# Revit family: Hager-Panelboard_Invicta_3_(630A-800A_Inc_125A_Out)-NoHosted-UK-en
name_source: partatom
category: Electrical Equipment
units: mm (PartAtom-declared; Revit-internal decimal feet)

## family parameters
Always vertical = Yes
Cut with Voids When Loaded = No
Panel Configuration = Two Columns, Circuits Across
Part Type = Panelboard
Room Calculation Point = No
Round Connector Dimension = Use Diameter
Shared = No
Work Plane-Based = Yes

## types (6) — shared parameters
Classification.Uniclass.Pr.Description = Control circuit device enclosures
Classification.Uniclass.Pr.Number = Pr_80_77_28_16
Default Elevation = 1219 mm
EF000003 - Mounting method = EV000384 - Surface mounted (plaster)
EF000007 - Colour = EV000154 - Other
EF000008 - Width = 900 mm  [stored 2.95276 ft]
EF000049 - Depth = 220 mm  [stored 0.721785 ft]
EF000118 - With mounting plate = No
EF000339 - Type of cover = EV004216 - Door
EF001062 - EMC-version = No
EF001088 - Extension possible = No
EF001134 - DIN-rail = No
EF001596 - Material housing = EV000179 - Steel
EF004462 - Type of closure = EV001412 - Cylinder
EF005474 - Degree of protection (IP) = EV006410 - IP30
EF006306 - With lock = Yes
EF015776 - Earthing terminal block = Yes
EF015777 - Neutral terminal block = Yes
EF015941 - Signal passing door = No
HG000002 - With door or cover = Yes
HG000003 - Range = Panelboards
HG000005 - Thickness = 3 mm  [stored 0.00984252 ft]
HG000017 - Distance between poles = 25 mm  [stored 0.082021 ft]
Manufacturer = Hager
Type Comments = Panelboards
zero-valued in all types: EF000218 - Built-in depth, EF000266 - Number of rows, EF000332 - Built-in height, EF000846 - Built-in width, EF001131 - Internal depth

## per-type parameters (varying)
| type | EF000040 - Height | EF002950 - Width in number of modular spacings | EF006244 - Transparent cover/door | HG000004 - Manufacturer reference | Model |
| Surface mounted IP30 W900 H1250 D220 12 Modular spacings - JF608B | 1250 mm  [stored 4.10105 ft] | 12 | No | JF608B | JF608B |
| Surface mounted IP30 W900 H1250 D220 12 Modular spacings - JF608BG | 1250 mm  [stored 4.10105 ft] | 12 | Yes | JF608BG | JF608BG |
| Surface mounted IP30 W900 H1400 D220 18 Modular spacings - JF812B | 1400 mm | 18 | No | JF812B | JF812B |
| Surface mounted IP30 W900 H1400 D220 18 Modular spacings - JF812BG | 1400 mm | 18 | Yes | JF812BG | JF812BG |
| Surface mounted IP30 W900 H1700 D220 27 Modular spacings - JF818B | 1700 mm  [stored 5.57743 ft] | 27 | No | JF818B | JF818B |
| Surface mounted IP30 W900 H1700 D220 27 Modular spacings - JF818BG | 1700 mm  [stored 5.57743 ft] | 27 | Yes | JF818BG | JF818BG |

note: [stored X ft] marks values corroborated as IEEE doubles in the binary element streams (Revit-internal decimal feet)

## geometry (parser evidence)
native form markers: Sweep x12
no freeform markers — native parametric forms only
